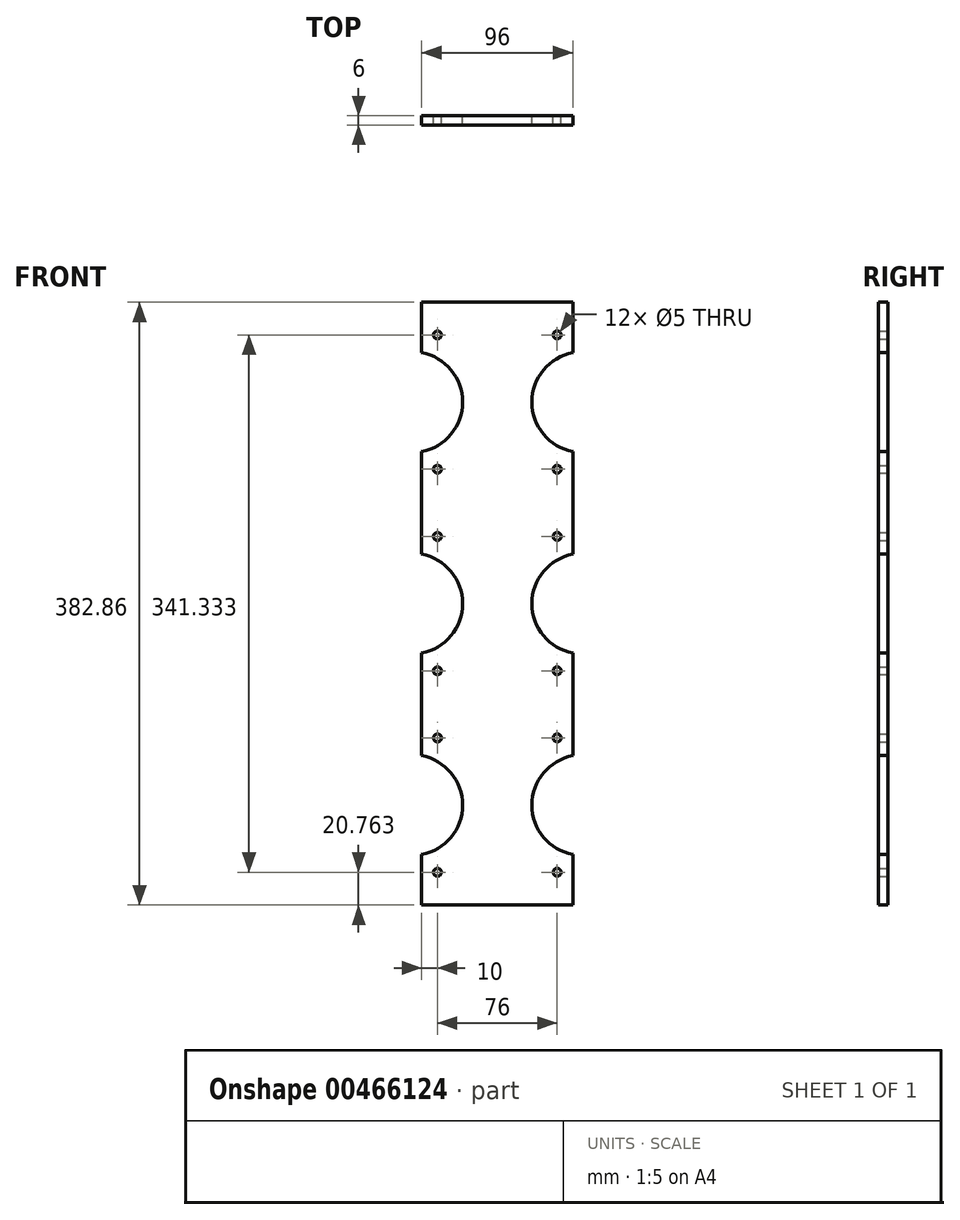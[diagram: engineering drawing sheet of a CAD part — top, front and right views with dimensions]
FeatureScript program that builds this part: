
annotation { "Feature Type Name" : "Feature", "Feature Type Description" : "" }
export const myFeature = defineFeature(function(context is Context, id is Id, definition is map)
    precondition{}
    {
        {
            var Q0;
            Q0=qCreatedBy(makeId("Front.planeOp"),FACE);
            var sketch = newSketch(context, id + "F0", { "sketchPlane" : qUnion([Q0])});
            skLineSegment(sketch, "E0", {"start": v(55, 96) * mm, "end": v(55, 32) * mm});
            skLineSegment(sketch, "E1", {"start": v(55, 32) * mm, "end": v(45, 32) * mm});
            skLineSegment(sketch, "E2", {"start": v(-55, 96) * mm, "end": v(-55, 32) * mm});
            skLineSegment(sketch, "E3", {"start": v(-55, 32) * mm, "end": v(-45, 32) * mm});
            skLineSegment(sketch, "E4", {"start": v(-45, -32) * mm, "end": v(-55, -32) * mm});
            skLineSegment(sketch, "E5", {"start": v(-55, -32) * mm, "end": v(-55, -64) * mm});
            skLineSegment(sketch, "E6", {"start": v(-55, -64) * mm, "end": v(55, -64) * mm});
            skLineSegment(sketch, "E7", {"start": v(55, -64) * mm, "end": v(55, -32) * mm});
            skLineSegment(sketch, "E8", {"start": v(55, -32) * mm, "end": v(45, -32) * mm});
            skArc(sketch, "E9", {"start": v(-45, 32) * mm, "mid": v(-13, 0) * mm, "end": v(-45, -32) * mm});
            skArc(sketch, "E10", {"start": v(45, 32) * mm, "mid": v(13, 0) * mm, "end": v(45, -32) * mm});
            skLineSegment(sketch, "E11", {"start": v(-45, -64) * mm, "end": v(-45, 192) * mm, "construction": true});
            skLineSegment(sketch, "E12", {"start": v(45, -64) * mm, "end": v(45, 192) * mm, "construction": true});
            skCircle(sketch, "E13", {"center": v(-45, 48) * mm, "radius": 2.5 * mm});
            skCircle(sketch, "E14", {"center": v(-45, -48) * mm, "radius": 2.5 * mm});
            skCircle(sketch, "E15", {"center": v(45, -48) * mm, "radius": 2.5 * mm});
            skCircle(sketch, "E16", {"center": v(45, 48) * mm, "radius": 2.5 * mm});
            skLineSegment(sketch, "E17.0.1.0", {"start": v(-45, 96) * mm, "end": v(-55, 96) * mm});
            skArc(sketch, "E17.0.1.1", {"start": v(-45, 160) * mm, "mid": v(-13, 128) * mm, "end": v(-45, 96) * mm});
            skLineSegment(sketch, "E17.0.1.2", {"start": v(-55, 160) * mm, "end": v(-45, 160) * mm});
            skLineSegment(sketch, "E17.0.1.3", {"start": v(55, 160) * mm, "end": v(45, 160) * mm});
            skArc(sketch, "E17.0.1.4", {"start": v(45, 160) * mm, "mid": v(13, 128) * mm, "end": v(45, 96) * mm});
            skLineSegment(sketch, "E17.0.1.5", {"start": v(55, 96) * mm, "end": v(45, 96) * mm});
            skLineSegment(sketch, "E17.direction1", {"start": v(-55, -32) * mm, "end": v(-30, -32) * mm, "construction": true});
            skLineSegment(sketch, "E17.direction2", {"start": v(-55, -32) * mm, "end": v(-55, 96) * mm, "construction": true});
            skLineSegment(sketch, "E18", {"start": v(-55, 160) * mm, "end": v(-55, 192) * mm});
            skLineSegment(sketch, "E19", {"start": v(-55, 192) * mm, "end": v(55, 192) * mm});
            skLineSegment(sketch, "E20", {"start": v(55, 192) * mm, "end": v(55, 160) * mm});
            skCircle(sketch, "E21", {"center": v(-45, 176) * mm, "radius": 2.5 * mm});
            skCircle(sketch, "E22", {"center": v(45, 176) * mm, "radius": 2.5 * mm});
            skCircle(sketch, "E23", {"center": v(45, 80) * mm, "radius": 2.5 * mm});
            skCircle(sketch, "E24", {"center": v(-45, 80) * mm, "radius": 2.5 * mm});
            skSolve(sketch);
        }
        {
            var Q0;
            Q0=qCreatedBy(makeId("Front.planeOp"),FACE);
            var sketch = newSketch(context, id + "F1", { "sketchPlane" : qUnion([Q0])});
            skLineSegment(sketch, "E25", {"start": v(-48, -159.43) * mm, "end": v(-48, -191.43) * mm});
            skLineSegment(sketch, "E26", {"start": v(-48, -191.43) * mm, "end": v(48, -191.43) * mm});
            skLineSegment(sketch, "E27", {"start": v(48, -191.43) * mm, "end": v(48, -159.43) * mm});
            skArc(sketch, "E28", {"start": v(-48, -96.57) * mm, "mid": v(-22, -128) * mm, "end": v(-48, -159.43) * mm});
            skArc(sketch, "E29", {"start": v(48, -96.57) * mm, "mid": v(22, -128) * mm, "end": v(48, -159.43) * mm});
            skLineSegment(sketch, "E30", {"start": v(-38, -191.43) * mm, "end": v(-38, 192) * mm, "construction": true});
            skLineSegment(sketch, "E31", {"start": v(38, -191.43) * mm, "end": v(38, 192) * mm, "construction": true});
            skCircle(sketch, "E32", {"center": v(-38, -85.33) * mm, "radius": 2.5 * mm});
            skCircle(sketch, "E33", {"center": v(-38, -170.67) * mm, "radius": 2.5 * mm});
            skCircle(sketch, "E34", {"center": v(38, -170.67) * mm, "radius": 2.5 * mm});
            skCircle(sketch, "E35", {"center": v(38, -85.33) * mm, "radius": 2.5 * mm});
            skCircle(sketch, "E36.0.1.0", {"center": v(38, -42.67) * mm, "radius": 2.5 * mm});
            skCircle(sketch, "E36.0.1.1", {"center": v(38, 42.67) * mm, "radius": 2.5 * mm});
            skArc(sketch, "E36.0.1.2", {"start": v(-48, 31.43) * mm, "mid": v(-22, 0) * mm, "end": v(-48, -31.43) * mm});
            skCircle(sketch, "E36.0.1.3", {"center": v(-38, -42.67) * mm, "radius": 2.5 * mm});
            skArc(sketch, "E36.0.1.4", {"start": v(48, 31.43) * mm, "mid": v(22, 0) * mm, "end": v(48, -31.43) * mm});
            skCircle(sketch, "E36.0.1.5", {"center": v(-38, 42.67) * mm, "radius": 2.5 * mm});
            skCircle(sketch, "E36.0.2.0", {"center": v(38, 85.33) * mm, "radius": 2.5 * mm});
            skCircle(sketch, "E36.0.2.1", {"center": v(38, 170.67) * mm, "radius": 2.5 * mm});
            skArc(sketch, "E36.0.2.2", {"start": v(-48, 159.43) * mm, "mid": v(-22, 128) * mm, "end": v(-48, 96.57) * mm});
            skCircle(sketch, "E36.0.2.3", {"center": v(-38, 85.33) * mm, "radius": 2.5 * mm});
            skArc(sketch, "E36.0.2.4", {"start": v(48, 159.43) * mm, "mid": v(22, 128) * mm, "end": v(48, 96.57) * mm});
            skCircle(sketch, "E36.0.2.5", {"center": v(-38, 170.67) * mm, "radius": 2.5 * mm});
            skLineSegment(sketch, "E36.direction1", {"start": v(-38, -170.67) * mm, "end": v(-13, -170.67) * mm, "construction": true});
            skLineSegment(sketch, "E36.direction2", {"start": v(-38, -170.67) * mm, "end": v(-38, -42.67) * mm, "construction": true});
            skLineSegment(sketch, "E37", {"start": v(-48, -96.57) * mm, "end": v(-48, -31.43) * mm});
            skLineSegment(sketch, "E38", {"start": v(-48, 31.43) * mm, "end": v(-48, 96.57) * mm});
            skLineSegment(sketch, "E39", {"start": v(48, 96.57) * mm, "end": v(48, 31.43) * mm});
            skLineSegment(sketch, "E40", {"start": v(48, -31.43) * mm, "end": v(48, -96.57) * mm});
            skLineSegment(sketch, "E41.MirrorCS", {"start": v(48, 191.43) * mm, "end": v(48, 159.43) * mm});
            skLineSegment(sketch, "E42.MirrorCS", {"start": v(-48, 159.43) * mm, "end": v(-48, 191.43) * mm});
            skLineSegment(sketch, "E43.MirrorCS", {"start": v(-48, 191.43) * mm, "end": v(48, 191.43) * mm});
            skLineSegment(sketch, "E44", {"start": v(-54, -128) * mm, "end": v(54, -128) * mm, "construction": true});
            skSolve(sketch);
        }
        {
            var Q0;
            Q0 = qSketchRegion(id + "F1", true);
            extrude(context, id + "F2", {"entities" : qUnion([Q0]), "depth" : 6 * mm, "offsetDistance" : 25 * mm});
        }
    });
